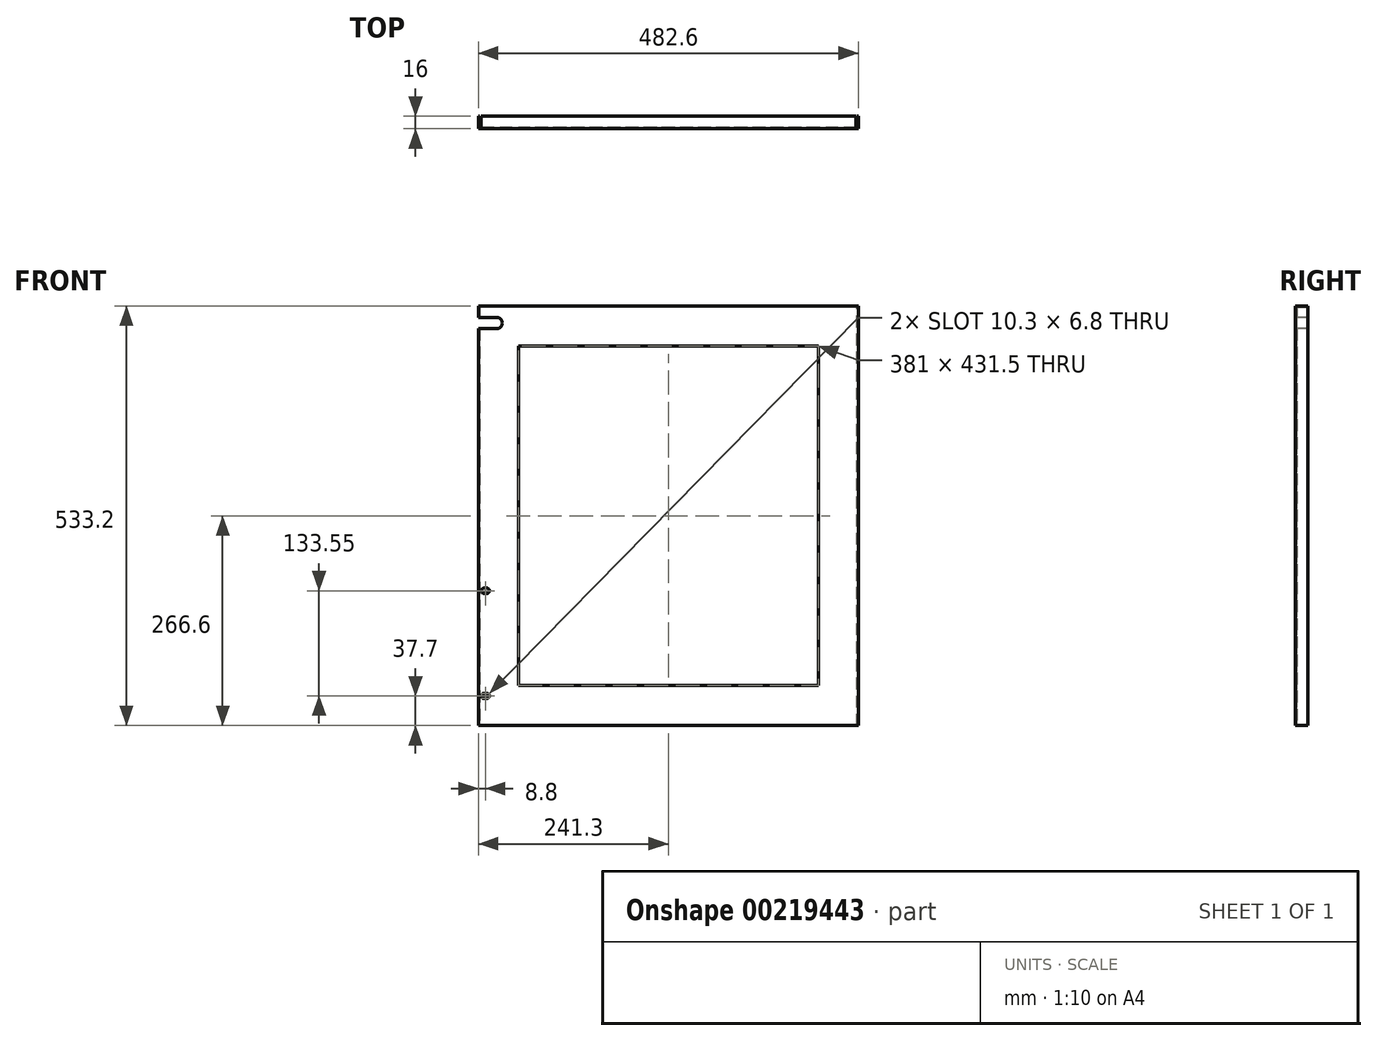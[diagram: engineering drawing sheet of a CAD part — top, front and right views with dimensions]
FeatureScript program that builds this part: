
annotation { "Feature Type Name" : "Feature", "Feature Type Description" : "" }
export const myFeature = defineFeature(function(context is Context, id is Id, definition is map)
    precondition{}
    {
        {
            var Q0;
            Q0=qCreatedBy(makeId("Front.planeOp"),FACE);
            var sketch = newSketch(context, id + "F0", { "sketchPlane" : qUnion([Q0])});
            skLineSegment(sketch, "E0.bottom", {"start": v(241.3, -266.6) * mm, "end": v(-241.3, -266.6) * mm});
            skLineSegment(sketch, "E0.top", {"start": v(241.3, 266.6) * mm, "end": v(-241.3, 266.6) * mm});
            skLineSegment(sketch, "E0.left", {"start": v(241.3, -266.6) * mm, "end": v(241.3, 266.6) * mm});
            skLineSegment(sketch, "E0.right", {"start": v(-241.3, -266.6) * mm, "end": v(-241.3, 266.6) * mm});
            skPoint(sketch, "E0.middle", {"position": v(0, 0) * mm});
            skSolve(sketch);
        }
        {
            var Q0;
            Q0=qSketchRegion(id+"F0",true);
            extrude(context, id + "F1", {"entities" : qUnion([Q0]), "oppositeDirection" : true, "depth" : 1.6 * mm});
        }
        {
            var Q0;
            Q0=makeQuery(id+"F1.opExtrude","SWEPT_FACE",FACE,{"disambiguationData":[OSD([sQuery(id+"F0.wireOp",EDGE,"E0.right")])]});
            var sketch = newSketch(context, id + "F2", { "sketchPlane" : qUnion([Q0])});
            skLineSegment(sketch, "E1.bottom", {"start": v(0, 266.6) * mm, "end": v(-16, 266.6) * mm});
            skLineSegment(sketch, "E1.top", {"start": v(0, -266.6) * mm, "end": v(-16, -266.6) * mm});
            skLineSegment(sketch, "E1.left", {"start": v(0, 266.6) * mm, "end": v(0, -266.6) * mm});
            skLineSegment(sketch, "E1.right", {"start": v(-16, 266.6) * mm, "end": v(-16, -266.6) * mm});
            skSolve(sketch);
        }
        {
            var Q0;
            Q0=qSketchRegion(id+"F2",true);
            extrude(context, id + "F3", {"entities" : qUnion([Q0]), "operationType" : NewBodyOperationType.ADD, "oppositeDirection" : true, "depth" : 1.6 * mm});
        }
        {
            var Q0;
            Q0=makeQuery(id+"F1.opExtrude","SWEPT_FACE",FACE,{"disambiguationData":[OSD([sQuery(id+"F0.wireOp",EDGE,"E0.left")])]});
            var sketch = newSketch(context, id + "F4", { "sketchPlane" : qUnion([Q0])});
            skLineSegment(sketch, "E2.bottom", {"start": v(0, 266.6) * mm, "end": v(16, 266.6) * mm});
            skLineSegment(sketch, "E2.top", {"start": v(0, -266.6) * mm, "end": v(16, -266.6) * mm});
            skLineSegment(sketch, "E2.left", {"start": v(0, 266.6) * mm, "end": v(0, -266.6) * mm});
            skLineSegment(sketch, "E2.right", {"start": v(16, 266.6) * mm, "end": v(16, -266.6) * mm});
            skSolve(sketch);
        }
        {
            var Q0;
            Q0=qSketchRegion(id+"F4",true);
            extrude(context, id + "F5", {"entities" : qUnion([Q0]), "operationType" : NewBodyOperationType.ADD, "oppositeDirection" : true, "depth" : 1.6 * mm});
        }
        {
            var Q0;
            Q0=makeQuery(id+"F5.boolean.opBoolean","MERGE",FACE,{"derivedFrom":[makeQuery(id+"F3.boolean.opBoolean","MERGE",FACE,{"derivedFrom":[makeQuery(id+"F1.opExtrude","SWEPT_FACE",FACE,{"disambiguationData":[OSD([sQuery(id+"F0.wireOp",EDGE,"E0.top")])]}),makeQuery(id+"F3.opExtrude","SWEPT_FACE",FACE,{"disambiguationData":[OSD([sQuery(id+"F2.wireOp",EDGE,"E1.bottom")])]})]}),makeQuery(id+"F5.opExtrude","SWEPT_FACE",FACE,{"disambiguationData":[OSD([sQuery(id+"F4.wireOp",EDGE,"E2.bottom")])]})]});
            var sketch = newSketch(context, id + "F6", { "sketchPlane" : qUnion([Q0])});
            skLineSegment(sketch, "E3.bottom", {"start": v(-238.3, 0) * mm, "end": v(238.3, 0) * mm});
            skLineSegment(sketch, "E3.top", {"start": v(-238.3, 16) * mm, "end": v(238.3, 16) * mm});
            skLineSegment(sketch, "E3.left", {"start": v(-238.3, 0) * mm, "end": v(-238.3, 16) * mm});
            skLineSegment(sketch, "E3.right", {"start": v(238.3, 0) * mm, "end": v(238.3, 16) * mm});
            skSolve(sketch);
        }
        {
            var Q0;
            Q0=qSketchRegion(id+"F6",true);
            extrude(context, id + "F7", {"entities" : qUnion([Q0]), "operationType" : NewBodyOperationType.ADD, "oppositeDirection" : true, "depth" : 1.6 * mm});
        }
        {
            var Q0;
            Q0=makeQuery(id+"F5.boolean.opBoolean","MERGE",FACE,{"derivedFrom":[makeQuery(id+"F3.boolean.opBoolean","MERGE",FACE,{"derivedFrom":[makeQuery(id+"F1.opExtrude","SWEPT_FACE",FACE,{"disambiguationData":[OSD([sQuery(id+"F0.wireOp",EDGE,"E0.bottom")])]}),makeQuery(id+"F3.opExtrude","SWEPT_FACE",FACE,{"disambiguationData":[OSD([sQuery(id+"F2.wireOp",EDGE,"E1.top")])]})]}),makeQuery(id+"F5.opExtrude","SWEPT_FACE",FACE,{"disambiguationData":[OSD([sQuery(id+"F4.wireOp",EDGE,"E2.top")])]})]});
            var sketch = newSketch(context, id + "F8", { "sketchPlane" : qUnion([Q0])});
            skLineSegment(sketch, "E4.bottom", {"start": v(238.3, 0) * mm, "end": v(-238.3, 0) * mm});
            skLineSegment(sketch, "E4.top", {"start": v(238.3, -16) * mm, "end": v(-238.3, -16) * mm});
            skLineSegment(sketch, "E4.left", {"start": v(238.3, 0) * mm, "end": v(238.3, -16) * mm});
            skLineSegment(sketch, "E4.right", {"start": v(-238.3, 0) * mm, "end": v(-238.3, -16) * mm});
            skSolve(sketch);
        }
        {
            var Q0;
            Q0=qSketchRegion(id+"F8",true);
            extrude(context, id + "F9", {"entities" : qUnion([Q0]), "operationType" : NewBodyOperationType.ADD, "oppositeDirection" : true, "depth" : 1.6 * mm});
        }
        {
            var Q0;
            Q0=makeQuery(id+"F1.opExtrude","CAP_FACE",FACE,{"disambiguationData":[OSD([sQuery(id+"F0.wireOp",EDGE,"E0.bottom"),sQuery(id+"F0.wireOp",EDGE,"E0.top"),sQuery(id+"F0.wireOp",EDGE,"E0.left"),sQuery(id+"F0.wireOp",EDGE,"E0.right")])],"isStart":true});
            var sketch = newSketch(context, id + "F10", { "sketchPlane" : qUnion([Q0])});
            skLineSegment(sketch, "E5.bottom", {"start": v(190.5, -215.75) * mm, "end": v(-190.5, -215.75) * mm});
            skLineSegment(sketch, "E5.top", {"start": v(190.5, 215.75) * mm, "end": v(-190.5, 215.75) * mm});
            skLineSegment(sketch, "E5.left", {"start": v(190.5, -215.75) * mm, "end": v(190.5, 215.75) * mm});
            skLineSegment(sketch, "E5.right", {"start": v(-190.5, -215.75) * mm, "end": v(-190.5, 215.75) * mm});
            skPoint(sketch, "E5.middle", {"position": v(0, 0) * mm});
            skSolve(sketch);
        }
        {
            var Q0;
            Q0=qSketchRegion(id+"F10",true);
            extrude(context, id + "F11", {"entities" : qUnion([Q0]), "operationType" : NewBodyOperationType.REMOVE, "oppositeDirection" : true, "depth" : 1.6 * mm});
        }
        {
            var Q0;
            Q0=makeQuery(id+"F1.opExtrude","CAP_FACE",FACE,{"disambiguationData":[OSD([sQuery(id+"F0.wireOp",EDGE,"E0.bottom"),sQuery(id+"F0.wireOp",EDGE,"E0.top"),sQuery(id+"F0.wireOp",EDGE,"E0.left"),sQuery(id+"F0.wireOp",EDGE,"E0.right")])],"isStart":true});
            var sketch = newSketch(context, id + "F12", { "sketchPlane" : qUnion([Q0])});
            skLineSegment(sketch, "E6.bottom", {"start": v(-230.75, -232.3) * mm, "end": v(-234.25, -232.3) * mm});
            skLineSegment(sketch, "E6.top", {"start": v(-230.75, -225.5) * mm, "end": v(-234.25, -225.5) * mm});
            skLineSegment(sketch, "E6.left", {"start": v(-230.75, -232.3) * mm, "end": v(-230.75, -225.5) * mm});
            skLineSegment(sketch, "E6.right", {"start": v(-234.25, -232.3) * mm, "end": v(-234.25, -225.5) * mm});
            skPoint(sketch, "E6.middle", {"position": v(-232.5, -228.9) * mm});
            skArc(sketch, "E7", {"start": v(-234.25, -225.5) * mm, "mid": v(-237.65, -228.9) * mm, "end": v(-234.25, -232.3) * mm});
            skArc(sketch, "E8", {"start": v(-230.75, -232.3) * mm, "mid": v(-227.35, -228.9) * mm, "end": v(-230.75, -225.5) * mm});
            skSolve(sketch);
        }
        {
            var Q0;
            Q0=qSketchRegion(id+"F12",true);
            extrude(context, id + "F13", {"entities" : qUnion([Q0]), "operationType" : NewBodyOperationType.REMOVE, "oppositeDirection" : true, "depth" : 1.6 * mm});
        }
        {
            var Q0;
            Q0=makeQuery(id+"F1.opExtrude","CAP_FACE",FACE,{"disambiguationData":[OSD([sQuery(id+"F0.wireOp",EDGE,"E0.bottom"),sQuery(id+"F0.wireOp",EDGE,"E0.top"),sQuery(id+"F0.wireOp",EDGE,"E0.left"),sQuery(id+"F0.wireOp",EDGE,"E0.right")])],"isStart":true});
            var sketch = newSketch(context, id + "F14", { "sketchPlane" : qUnion([Q0])});
            skLineSegment(sketch, "E9.bottom", {"start": v(-230.75, -98.75) * mm, "end": v(-234.25, -98.75) * mm});
            skLineSegment(sketch, "E9.top", {"start": v(-230.75, -91.95) * mm, "end": v(-234.25, -91.95) * mm});
            skLineSegment(sketch, "E9.left", {"start": v(-230.75, -98.75) * mm, "end": v(-230.75, -91.95) * mm});
            skLineSegment(sketch, "E9.right", {"start": v(-234.25, -98.75) * mm, "end": v(-234.25, -91.95) * mm});
            skPoint(sketch, "E9.middle", {"position": v(-232.5, -95.35) * mm});
            skArc(sketch, "E10", {"start": v(-234.25, -91.95) * mm, "mid": v(-237.65, -95.35) * mm, "end": v(-234.25, -98.75) * mm});
            skArc(sketch, "E11", {"start": v(-230.75, -98.75) * mm, "mid": v(-227.35, -95.35) * mm, "end": v(-230.75, -91.95) * mm});
            skSolve(sketch);
        }
        {
            var Q0;
            Q0=qSketchRegion(id+"F14",true);
            extrude(context, id + "F15", {"entities" : qUnion([Q0]), "operationType" : NewBodyOperationType.REMOVE, "oppositeDirection" : true, "depth" : 1.6 * mm});
        }
        {
            var Q0;
            Q0=makeQuery(id+"F1.opExtrude","CAP_FACE",FACE,{"disambiguationData":[OSD([sQuery(id+"F0.wireOp",EDGE,"E0.bottom"),sQuery(id+"F0.wireOp",EDGE,"E0.top"),sQuery(id+"F0.wireOp",EDGE,"E0.left"),sQuery(id+"F0.wireOp",EDGE,"E0.right")])],"isStart":true});
            var sketch = newSketch(context, id + "F16", { "sketchPlane" : qUnion([Q0])});
            skLineSegment(sketch, "E12.bottom", {"start": v(-241.3, 237.8) * mm, "end": v(-218, 237.8) * mm});
            skLineSegment(sketch, "E12.top", {"start": v(-241.3, 251.8) * mm, "end": v(-218, 251.8) * mm});
            skLineSegment(sketch, "E12.left", {"start": v(-241.3, 237.8) * mm, "end": v(-241.3, 251.8) * mm});
            skLineSegment(sketch, "E12.right", {"start": v(-218, 237.8) * mm, "end": v(-218, 251.8) * mm});
            skArc(sketch, "E13", {"start": v(-218, 237.8) * mm, "mid": v(-211, 244.8) * mm, "end": v(-218, 251.8) * mm});
            skSolve(sketch);
        }
        {
            var Q0;
            Q0=qSketchRegion(id+"F16",true);
            extrude(context, id + "F17", {"entities" : qUnion([Q0]), "operationType" : NewBodyOperationType.REMOVE, "oppositeDirection" : true, "depth" : 16 * mm});
        }
    });
